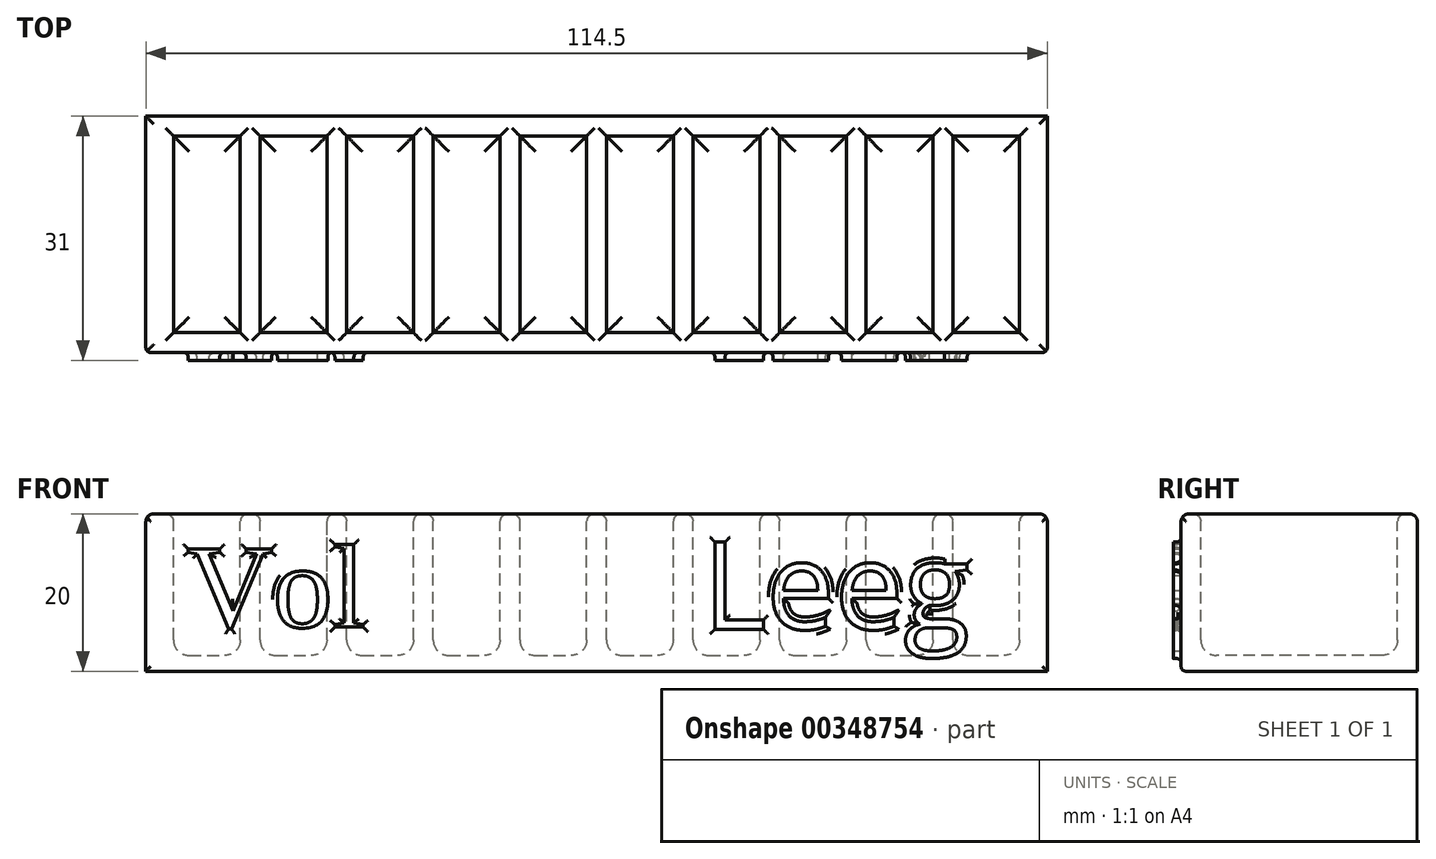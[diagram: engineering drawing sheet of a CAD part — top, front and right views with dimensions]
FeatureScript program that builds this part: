
annotation { "Feature Type Name" : "Feature", "Feature Type Description" : "" }
export const myFeature = defineFeature(function(context is Context, id is Id, definition is map)
    precondition{}
    {
        {
            var Q0;
            Q0=qCreatedBy(makeId("Top.planeOp"),FACE);
            var sketch = newSketch(context, id + "F0", { "sketchPlane" : qUnion([Q0])});
            skLineSegment(sketch, "E0.bottom", {"start": v(-30.51, 14.26) * mm, "end": v(83.99, 14.26) * mm});
            skLineSegment(sketch, "E0.top", {"start": v(-30.51, -15.74) * mm, "end": v(83.99, -15.74) * mm});
            skLineSegment(sketch, "E0.left", {"start": v(-30.51, 14.26) * mm, "end": v(-30.51, -15.74) * mm});
            skLineSegment(sketch, "E0.right", {"start": v(83.99, 14.26) * mm, "end": v(83.99, -15.74) * mm});
            skSolve(sketch);
        }
        {
            var Q0;
            Q0=makeQuery(id+"F0.imprint","IMPRINT",FACE,{"disambiguationData":[TD([[makeQuery(id+"F0.imprint","IMPRINT",EDGE,{"derivedFrom":sQuery(id+"F0.wireOp",EDGE,"E0.bottom")}),-1.0]])]});
            extrude(context, id + "F1", {"entities" : qUnion([Q0]), "depth" : 20 * mm});
        }
        {
            var Q0;
            Q0=makeQuery(id+"F1.opExtrude","CAP_FACE",FACE,{"disambiguationData":[OSD([sQuery(id+"F0.wireOp",EDGE,"E0.bottom"),sQuery(id+"F0.wireOp",EDGE,"E0.top"),sQuery(id+"F0.wireOp",EDGE,"E0.left"),sQuery(id+"F0.wireOp",EDGE,"E0.right")])],"isStart":false});
            var sketch = newSketch(context, id + "F2", { "sketchPlane" : qUnion([Q0])});
            skLineSegment(sketch, "E1.bottom", {"start": v(-27.01, 11.76) * mm, "end": v(-18.51, 11.76) * mm});
            skLineSegment(sketch, "E1.top", {"start": v(-27.01, -13.24) * mm, "end": v(-18.51, -13.24) * mm});
            skLineSegment(sketch, "E1.left", {"start": v(-27.01, 11.76) * mm, "end": v(-27.01, -13.24) * mm});
            skLineSegment(sketch, "E1.right", {"start": v(-18.51, 11.76) * mm, "end": v(-18.51, -13.24) * mm});
            skLineSegment(sketch, "E2.1.0.0", {"start": v(-7.51, 11.76) * mm, "end": v(-7.51, -13.24) * mm});
            skLineSegment(sketch, "E2.1.0.1", {"start": v(-16.01, 11.76) * mm, "end": v(-16.01, -13.24) * mm});
            skLineSegment(sketch, "E2.1.0.2", {"start": v(-16.01, -13.24) * mm, "end": v(-7.51, -13.24) * mm});
            skLineSegment(sketch, "E2.1.0.3", {"start": v(-16.01, 11.76) * mm, "end": v(-7.51, 11.76) * mm});
            skLineSegment(sketch, "E2.2.0.0", {"start": v(3.49, 11.76) * mm, "end": v(3.49, -13.24) * mm});
            skLineSegment(sketch, "E2.2.0.1", {"start": v(-5.01, 11.76) * mm, "end": v(-5.01, -13.24) * mm});
            skLineSegment(sketch, "E2.2.0.2", {"start": v(-5.01, -13.24) * mm, "end": v(3.49, -13.24) * mm});
            skLineSegment(sketch, "E2.2.0.3", {"start": v(-5.01, 11.76) * mm, "end": v(3.49, 11.76) * mm});
            skLineSegment(sketch, "E2.3.0.0", {"start": v(14.49, 11.76) * mm, "end": v(14.49, -13.24) * mm});
            skLineSegment(sketch, "E2.3.0.1", {"start": v(5.99, 11.76) * mm, "end": v(5.99, -13.24) * mm});
            skLineSegment(sketch, "E2.3.0.2", {"start": v(5.99, -13.24) * mm, "end": v(14.49, -13.24) * mm});
            skLineSegment(sketch, "E2.3.0.3", {"start": v(5.99, 11.76) * mm, "end": v(14.49, 11.76) * mm});
            skLineSegment(sketch, "E2.4.0.0", {"start": v(25.49, 11.76) * mm, "end": v(25.49, -13.24) * mm});
            skLineSegment(sketch, "E2.4.0.1", {"start": v(16.99, 11.76) * mm, "end": v(16.99, -13.24) * mm});
            skLineSegment(sketch, "E2.4.0.2", {"start": v(16.99, -13.24) * mm, "end": v(25.49, -13.24) * mm});
            skLineSegment(sketch, "E2.4.0.3", {"start": v(16.99, 11.76) * mm, "end": v(25.49, 11.76) * mm});
            skLineSegment(sketch, "E2.5.0.0", {"start": v(36.49, 11.76) * mm, "end": v(36.49, -13.24) * mm});
            skLineSegment(sketch, "E2.5.0.1", {"start": v(27.99, 11.76) * mm, "end": v(27.99, -13.24) * mm});
            skLineSegment(sketch, "E2.5.0.2", {"start": v(27.99, -13.24) * mm, "end": v(36.49, -13.24) * mm});
            skLineSegment(sketch, "E2.5.0.3", {"start": v(27.99, 11.76) * mm, "end": v(36.49, 11.76) * mm});
            skLineSegment(sketch, "E2.6.0.0", {"start": v(47.49, 11.76) * mm, "end": v(47.49, -13.24) * mm});
            skLineSegment(sketch, "E2.6.0.1", {"start": v(38.99, 11.76) * mm, "end": v(38.99, -13.24) * mm});
            skLineSegment(sketch, "E2.6.0.2", {"start": v(38.99, -13.24) * mm, "end": v(47.49, -13.24) * mm});
            skLineSegment(sketch, "E2.6.0.3", {"start": v(38.99, 11.76) * mm, "end": v(47.49, 11.76) * mm});
            skLineSegment(sketch, "E2.7.0.0", {"start": v(58.49, 11.76) * mm, "end": v(58.49, -13.24) * mm});
            skLineSegment(sketch, "E2.7.0.1", {"start": v(49.99, 11.76) * mm, "end": v(49.99, -13.24) * mm});
            skLineSegment(sketch, "E2.7.0.2", {"start": v(49.99, -13.24) * mm, "end": v(58.49, -13.24) * mm});
            skLineSegment(sketch, "E2.7.0.3", {"start": v(49.99, 11.76) * mm, "end": v(58.49, 11.76) * mm});
            skLineSegment(sketch, "E2.8.0.0", {"start": v(69.49, 11.76) * mm, "end": v(69.49, -13.24) * mm});
            skLineSegment(sketch, "E2.8.0.1", {"start": v(60.99, 11.76) * mm, "end": v(60.99, -13.24) * mm});
            skLineSegment(sketch, "E2.8.0.2", {"start": v(60.99, -13.24) * mm, "end": v(69.49, -13.24) * mm});
            skLineSegment(sketch, "E2.8.0.3", {"start": v(60.99, 11.76) * mm, "end": v(69.49, 11.76) * mm});
            skLineSegment(sketch, "E2.9.0.0", {"start": v(80.49, 11.76) * mm, "end": v(80.49, -13.24) * mm});
            skLineSegment(sketch, "E2.9.0.1", {"start": v(71.99, 11.76) * mm, "end": v(71.99, -13.24) * mm});
            skLineSegment(sketch, "E2.9.0.2", {"start": v(71.99, -13.24) * mm, "end": v(80.49, -13.24) * mm});
            skLineSegment(sketch, "E2.9.0.3", {"start": v(71.99, 11.76) * mm, "end": v(80.49, 11.76) * mm});
            skLineSegment(sketch, "E2.direction1", {"start": v(-27.01, -13.24) * mm, "end": v(-16.01, -13.24) * mm, "construction": true});
            skSolve(sketch);
        }
        {
            var Q0;
            Q0 = qSketchRegion(id + "F2", true);
            extrude(context, id + "F3", {"entities" : qUnion([Q0]), "operationType" : NewBodyOperationType.REMOVE, "oppositeDirection" : true, "depth" : 18 * mm});
        }
        {
            var Q0;
            Q0=makeQuery(id+"F3.boolean.opBoolean","COPY",FACE,{"derivedFrom":makeQuery(id+"F3.opExtrude","CAP_FACE",FACE,{"disambiguationData":[OSD([sQuery(id+"F2.wireOp",EDGE,"E1.bottom"),sQuery(id+"F2.wireOp",EDGE,"E1.top"),sQuery(id+"F2.wireOp",EDGE,"E1.left"),sQuery(id+"F2.wireOp",EDGE,"E1.right")])],"isStart":false})});
            var Q1;
            Q1=makeQuery(id+"F3.boolean.opBoolean","COPY",FACE,{"derivedFrom":makeQuery(id+"F3.opExtrude","CAP_FACE",FACE,{"disambiguationData":[OSD([sQuery(id+"F2.wireOp",EDGE,"E2.1.0.0"),sQuery(id+"F2.wireOp",EDGE,"E2.1.0.1"),sQuery(id+"F2.wireOp",EDGE,"E2.1.0.2"),sQuery(id+"F2.wireOp",EDGE,"E2.1.0.3")])],"isStart":false})});
            var Q2;
            Q2=makeQuery(id+"F3.boolean.opBoolean","COPY",FACE,{"derivedFrom":makeQuery(id+"F3.opExtrude","CAP_FACE",FACE,{"disambiguationData":[OSD([sQuery(id+"F2.wireOp",EDGE,"E2.2.0.0"),sQuery(id+"F2.wireOp",EDGE,"E2.2.0.1"),sQuery(id+"F2.wireOp",EDGE,"E2.2.0.2"),sQuery(id+"F2.wireOp",EDGE,"E2.2.0.3")])],"isStart":false})});
            var Q3;
            Q3=makeQuery(id+"F3.boolean.opBoolean","COPY",FACE,{"derivedFrom":makeQuery(id+"F3.opExtrude","CAP_FACE",FACE,{"disambiguationData":[OSD([sQuery(id+"F2.wireOp",EDGE,"E2.3.0.0"),sQuery(id+"F2.wireOp",EDGE,"E2.3.0.1"),sQuery(id+"F2.wireOp",EDGE,"E2.3.0.2"),sQuery(id+"F2.wireOp",EDGE,"E2.3.0.3")])],"isStart":false})});
            var Q4;
            Q4=makeQuery(id+"F3.boolean.opBoolean","COPY",FACE,{"derivedFrom":makeQuery(id+"F3.opExtrude","CAP_FACE",FACE,{"disambiguationData":[OSD([sQuery(id+"F2.wireOp",EDGE,"E2.4.0.0"),sQuery(id+"F2.wireOp",EDGE,"E2.4.0.1"),sQuery(id+"F2.wireOp",EDGE,"E2.4.0.2"),sQuery(id+"F2.wireOp",EDGE,"E2.4.0.3")])],"isStart":false})});
            var Q5;
            Q5=makeQuery(id+"F3.boolean.opBoolean","COPY",FACE,{"derivedFrom":makeQuery(id+"F3.opExtrude","CAP_FACE",FACE,{"disambiguationData":[OSD([sQuery(id+"F2.wireOp",EDGE,"E2.5.0.0"),sQuery(id+"F2.wireOp",EDGE,"E2.5.0.1"),sQuery(id+"F2.wireOp",EDGE,"E2.5.0.2"),sQuery(id+"F2.wireOp",EDGE,"E2.5.0.3")])],"isStart":false})});
            var Q6;
            Q6=makeQuery(id+"F3.boolean.opBoolean","COPY",FACE,{"derivedFrom":makeQuery(id+"F3.opExtrude","CAP_FACE",FACE,{"disambiguationData":[OSD([sQuery(id+"F2.wireOp",EDGE,"E2.6.0.0"),sQuery(id+"F2.wireOp",EDGE,"E2.6.0.1"),sQuery(id+"F2.wireOp",EDGE,"E2.6.0.2"),sQuery(id+"F2.wireOp",EDGE,"E2.6.0.3")])],"isStart":false})});
            var Q7;
            Q7=makeQuery(id+"F3.boolean.opBoolean","COPY",FACE,{"derivedFrom":makeQuery(id+"F3.opExtrude","CAP_FACE",FACE,{"disambiguationData":[OSD([sQuery(id+"F2.wireOp",EDGE,"E2.7.0.0"),sQuery(id+"F2.wireOp",EDGE,"E2.7.0.1"),sQuery(id+"F2.wireOp",EDGE,"E2.7.0.2"),sQuery(id+"F2.wireOp",EDGE,"E2.7.0.3")])],"isStart":false})});
            var Q8;
            Q8=makeQuery(id+"F3.boolean.opBoolean","COPY",FACE,{"derivedFrom":makeQuery(id+"F3.opExtrude","CAP_FACE",FACE,{"disambiguationData":[OSD([sQuery(id+"F2.wireOp",EDGE,"E2.8.0.0"),sQuery(id+"F2.wireOp",EDGE,"E2.8.0.1"),sQuery(id+"F2.wireOp",EDGE,"E2.8.0.2"),sQuery(id+"F2.wireOp",EDGE,"E2.8.0.3")])],"isStart":false})});
            var Q9;
            Q9=makeQuery(id+"F3.boolean.opBoolean","COPY",FACE,{"derivedFrom":makeQuery(id+"F3.opExtrude","CAP_FACE",FACE,{"disambiguationData":[OSD([sQuery(id+"F2.wireOp",EDGE,"E2.9.0.0"),sQuery(id+"F2.wireOp",EDGE,"E2.9.0.1"),sQuery(id+"F2.wireOp",EDGE,"E2.9.0.2"),sQuery(id+"F2.wireOp",EDGE,"E2.9.0.3")])],"isStart":false})});
            fillet(context, id + "F4", {"entities" : qUnion([Q0, Q1, Q2, Q3, Q4, Q5, Q6, Q7, Q8, Q9]), "radius" : 2 * mm, "tangentPropagation" : true, "allowEdgeOverflow" : false});
        }
        {
            var Q0;
            Q0=makeQuery(id+"F1.opExtrude","CAP_FACE",FACE,{"disambiguationData":[OSD([sQuery(id+"F0.wireOp",EDGE,"E0.bottom"),sQuery(id+"F0.wireOp",EDGE,"E0.top"),sQuery(id+"F0.wireOp",EDGE,"E0.left"),sQuery(id+"F0.wireOp",EDGE,"E0.right")])],"isStart":false});
            fillet(context, id + "F5", {"entities" : qUnion([Q0]), "radius" : 1 * mm, "tangentPropagation" : true, "allowEdgeOverflow" : false});
        }
        {
            var Q0;
            Q0=makeQuery(id+"F1.opExtrude","SWEPT_FACE",FACE,{"disambiguationData":[OSD([sQuery(id+"F0.wireOp",EDGE,"E0.top")])]});
            var sketch = newSketch(context, id + "F6", { "sketchPlane" : qUnion([Q0])});
            skText(sketch, "E3", { "text": "Vol", "fontName": "Tinos-Regular.ttf"});
            skText(sketch, "E4", { "text": "Leeg", "fontName": "OpenSans-Regular.ttf"});
            const initialGuessF6  = {"E3": [-0.02531, 0.0056, 1, 0, 0.0109], "E4": [0.04025, 0.00534, 1, 0, 0.01116]};
            skSetInitialGuess(sketch, initialGuessF6);
            skSolve(sketch);
        }
        {
            var Q0;
            Q0 = qSketchRegion(id + "F6", true);
            extrude(context, id + "F7", {"entities" : qUnion([Q0]), "operationType" : NewBodyOperationType.ADD, "depth" : 1 * mm});
        }
        {
            var Q0;
            {var subQ1=sQuery(id+"F0.wireOp",EDGE,"E0.left");var subQ2=sQuery(id+"F0.wireOp",EDGE,"E0.top");Q0=makeQuery(id+"F7.boolean.opBoolean","SPLIT",FACE,{"disambiguationData":[TD([makeQuery(id+"F1.opExtrude","SWEPT_FACE",FACE,{"disambiguationData":[OSD([subQ1])]})])],"derivedFrom":makeQuery(id+"F1.opExtrude","SWEPT_FACE",FACE,{"disambiguationData":[OSD([subQ2])]})});}
            fillet(context, id + "F8", {"entities" : qUnion([Q0]), "radius" : 0.6 * mm, "allowEdgeOverflow" : false});
        }
    });
